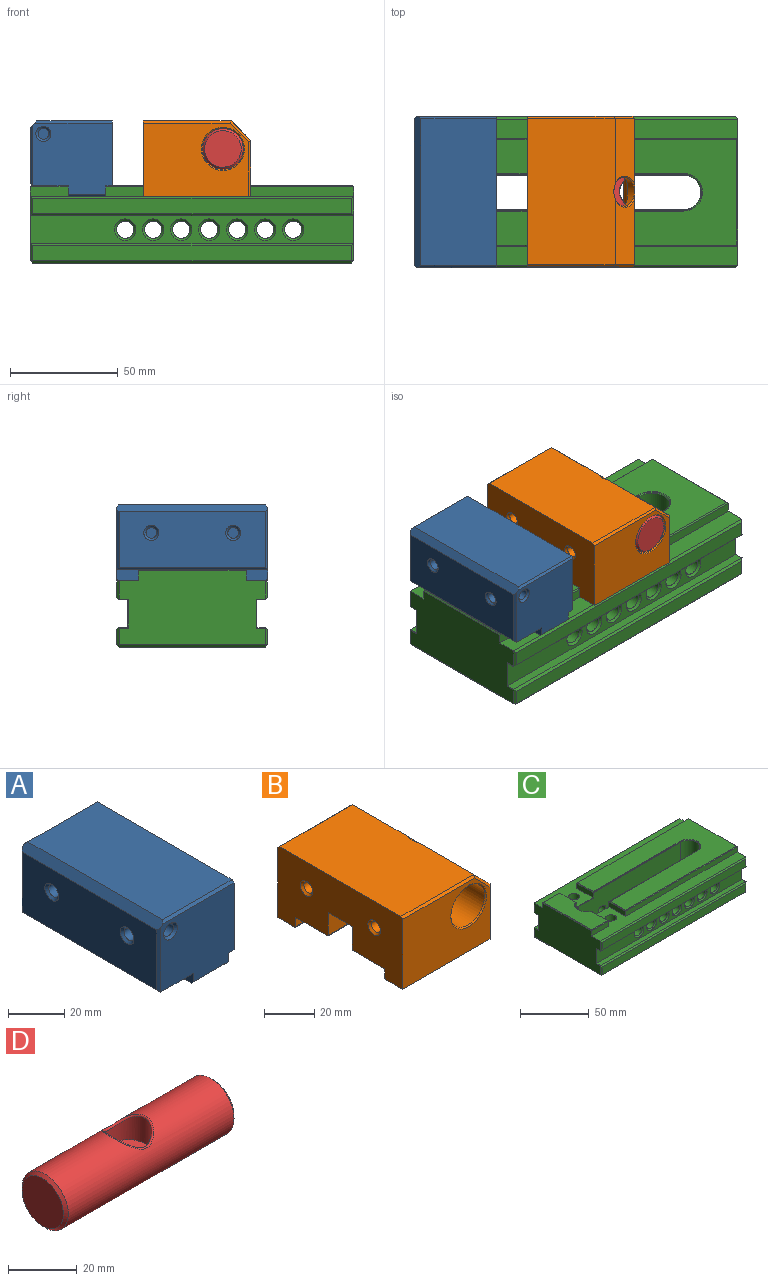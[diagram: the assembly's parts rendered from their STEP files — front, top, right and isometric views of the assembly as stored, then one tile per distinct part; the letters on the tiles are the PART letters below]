
ASSEMBLY  parts=4 mates=3
PART A: 42 faces, bbox 38x70x35 mm
  f0: plane 70x16.5mm, normal (0,0,-1), area 1155mm2, adj f1,f8,f9,f39
  f1: plane 70x4.8mm, normal (-1,0,0), area 335mm2, adj f0,f2,f8,f9,f40,f41
  f2: plane 68x17.5mm, normal (0,0,-1), area 1113mm2, adj f1,f3,f31,f32,f40,f41
  f3: plane 70x4.8mm, normal (1,0,0), area 335mm2, adj f2,f4,f8,f9,f40,f41
  f4: plane 70x3mm, normal (0,0,-1), area 210mm2, adj f3,f5,f8,f9
  f5: plane 70x30.2mm, normal (1,0,0), area 2036mm2, adj f4,f6,f8,f9,f11,f12,f33,f34
  f6: plane 68x35mm, normal (0,0,1), area 2380mm2, adj f5,f10,f11,f12
  f7: plane 68x26.2mm, normal (-1,0,0), area 1704.6mm2, adj f10,f13,f14,f37,f38,f39
  f8: plane 37x33mm, normal (0,1,0), area 1107.9mm2, adj f0,f1,f3,f4,f5,f10,f11,f13
  f9: plane 37x33mm, normal (0,-1,0), area 1107.9mm2, adj f0,f1,f3,f4,f5,f10,f12,f14
  f10: plane 70x3mm, normal (-0.71,0,0.71), area 294.2mm2, adj f6,f7,f8,f9,f11,f12,f13,f14
  f11: plane 36x1mm, normal (0,0.71,0.71), area 50.2mm2, adj f5,f6,f8,f10
  f12: plane 36x1mm, normal (0,-0.71,0.71), area 50.2mm2, adj f5,f6,f9,f10
  f13: plane 28.2x1mm, normal (-0.71,0.71,0), area 38.5mm2, adj f7,f8,f10,f39
  f14: plane 28.2x1mm, normal (-0.71,-0.71,0), area 38.5mm2, adj f7,f9,f10,f39
  f15: cylinder r=2.5mm len=14mm, axis (0,-1,0), area 219.9mm2, adj f16,f35
  f16: plane 5x5mm, normal (0,-1,0), area 19.6mm2, adj f15
  f17: cylinder r=2.5mm len=14mm, axis (0,-1,0), area 219.9mm2, adj f18,f36
  f18: plane 5x5mm, normal (0,1,0), area 19.6mm2, adj f17
  f19: cylinder r=2.5mm len=18.18mm, axis (0,0,-1), area 285.5mm2, adj f20,f32
  f20: plane 5x5mm, normal (0,0,-1), area 19.6mm2, adj f19
  f21: cylinder r=2.5mm len=18.18mm, axis (0,0,-1), area 285.5mm2, adj f22,f31
  f22: plane 5x5mm, normal (0,0,-1), area 19.6mm2, adj f21
  f23: cylinder r=2.5mm len=14mm, axis (1,0,0), area 219.9mm2, adj f24,f33
  f24: plane 5x5mm, normal (1,0,0), area 19.6mm2, adj f23
  f25: cylinder r=2.5mm len=14mm, axis (1,0,0), area 219.9mm2, adj f26,f34
  f26: plane 5x5mm, normal (1,0,0), area 19.6mm2, adj f25
  f27: cylinder r=2.5mm len=7mm, axis (1,0,0), area 110mm2, adj f28,f38
  f28: plane 5x5mm, normal (-1,0,0), area 19.6mm2, adj f27
  f29: cylinder r=2.5mm len=7mm, axis (1,0,0), area 110mm2, adj f30,f37
  f30: plane 5x5mm, normal (-1,0,0), area 19.6mm2, adj f29
  f31: cone r=3.5mm half-angle=45deg, axis (0,0,-1), area 26.7mm2, adj f2,f21
  f32: cone r=3.5mm half-angle=45deg, axis (0,0,-1), area 26.7mm2, adj f2,f19
  f33: cone r=2.5mm half-angle=45deg, axis (1,0,0), area 26.7mm2, adj f5,f23
  f34: cone r=2.5mm half-angle=45deg, axis (1,0,0), area 26.7mm2, adj f5,f25
  f35: cone r=2.5mm half-angle=45deg, axis (0,-1,0), area 26.7mm2, adj f9,f15
  f36: cone r=3.5mm half-angle=45deg, axis (0,1,0), area 26.7mm2, adj f8,f17
  f37: cone r=2.5mm half-angle=45deg, axis (-1,0,0), area 26.7mm2, adj f7,f29
  f38: cone r=2.5mm half-angle=45deg, axis (-1,0,0), area 26.7mm2, adj f7,f27
  f39: plane 70x1mm, normal (-0.71,0,-0.71), area 97.6mm2, adj f0,f7,f13,f14
  f40: plane 17.5x1mm, normal (0,0.71,-0.71), area 24.7mm2, adj f1,f2,f3,f8
  f41: plane 17.5x1mm, normal (0,-0.71,-0.71), area 24.7mm2, adj f1,f2,f3,f9
PART B: 38 faces, bbox 50.5x70x35.6 mm
  f0: plane 30.91x9.19mm, normal (0.71,0,0.71), area 362.7mm2, adj f3,f6,f23,f31
  f1: plane 30.91x9.19mm, normal (0.71,0,0.71), area 362.7mm2, adj f3,f6,f20,f31
  f2: plane 50x9.5mm, normal (0,0,-1), area 474.5mm2, adj f4,f6,f9,f19,f24
  f3: plane 68x40.81mm, normal (0,0,1), area 2772.4mm2, adj f0,f1,f4,f18,f21,f31
  f4: plane 70x35mm, normal (-1,0,0), area 1967.6mm2, adj f2,f3,f5,f8,f9,f10,f11,f13
  f5: plane 50x9.5mm, normal (0,0,-1), area 474.5mm2, adj f4,f6,f8,f22,f25
  f6: plane 68x25.81mm, normal (1,0,0), area 1348.4mm2, adj f0,f1,f2,f5,f10,f12,f13,f14
  f7: cylinder r=9.5mm len=69mm, axis (0,-1,0), area 3721.9mm2, adj f10,f11,f12,f13,f28,f29,f30
  f8: plane 49x34mm, normal (0,1,0), area 1314.8mm2, adj f4,f5,f21,f22,f23,f28
  f9: plane 49x34mm, normal (0,-1,0), area 1314.8mm2, adj f2,f4,f18,f19,f20,f29
  f10: plane 50x10.93mm, normal (0,-1,0), area 504mm2, adj f4,f6,f7,f11,f12,f26
  f11: plane 29.31x13.5mm, normal (0,0,-1), area 395.6mm2, adj f4,f7,f10,f13
  f12: plane 13.5x5.31mm, normal (0,0,-1), area 71.6mm2, adj f6,f7,f10,f13
  f13: plane 50x10.93mm, normal (0,1,0), area 504mm2, adj f4,f6,f7,f11,f12,f27
  f14: plane 50x4.5mm, normal (0,1,0), area 225mm2, adj f4,f6,f17,f24
  f15: plane 50x4.5mm, normal (0,-1,0), area 225mm2, adj f4,f6,f16,f25
  f16: plane 50x17.75mm, normal (0,0,-1), area 887.5mm2, adj f4,f6,f15,f26
  f17: plane 50x17.75mm, normal (0,0,-1), area 887.5mm2, adj f4,f6,f14,f27
  f18: plane 40.81x1mm, normal (0,-0.71,0.71), area 57.4mm2, adj f3,f4,f9,f20
  f19: plane 25.81x1mm, normal (0.71,-0.71,0), area 36.2mm2, adj f2,f6,f9,f20
  f20: plane 9.61x9.61mm, normal (0.5,-0.71,0.5), area 17.8mm2, adj f1,f9,f18,f19
  f21: plane 40.81x1mm, normal (0,0.71,0.71), area 57.4mm2, adj f3,f4,f8,f23
  f22: plane 25.81x1mm, normal (0.71,0.71,0), area 36.2mm2, adj f5,f6,f8,f23
  f23: plane 9.61x9.61mm, normal (0.5,0.71,0.5), area 17.8mm2, adj f0,f8,f21,f22
  f24: cylinder r=0.5mm len=50mm, axis (1,0,0), area 39.3mm2, adj f2,f4,f6,f14
  f25: cylinder r=0.5mm len=50mm, axis (-1,0,0), area 39.3mm2, adj f4,f5,f6,f15
  f26: cylinder r=0.5mm len=50mm, axis (-1,0,0), area 39.3mm2, adj f4,f6,f10,f16
  f27: cylinder r=0.5mm len=50mm, axis (-1,0,0), area 39.3mm2, adj f4,f6,f13,f17
  f28: cone r=10mm half-angle=45deg, axis (0,1,0), area 43.3mm2, adj f7,f8
  f29: cone r=9.5mm half-angle=45deg, axis (0,-1,0), area 43.3mm2, adj f7,f9
  f30: cylinder r=6.75mm len=13.5mm, axis (0.71,0,0.71), area 137mm2, adj f7,f31
  f31: cone r=6.75mm half-angle=45deg, axis (0.71,0,0.71), area 26.4mm2, adj f0,f1,f3,f6,f30
  f32: cylinder r=2.5mm len=14mm, axis (-1,0,0), area 219.9mm2, adj f33,f36
  f33: plane 5x5mm, normal (-1,0,0), area 19.6mm2, adj f32
  f34: cylinder r=2.5mm len=14mm, axis (-1,0,0), area 219.9mm2, adj f35,f37
  f35: plane 5x5mm, normal (-1,0,0), area 19.6mm2, adj f34
  f36: cone r=3.5mm half-angle=45deg, axis (-1,0,0), area 26.7mm2, adj f4,f32
  f37: cone r=3.5mm half-angle=45deg, axis (-1,0,0), area 26.7mm2, adj f4,f34
PART C: 125 faces, bbox 150x70x36 mm
  f0: plane 150x26.23mm, normal (0,0,1), area 1594.1mm2, adj f12,f13,f28,f29,f30,f31,f44,f79
  f1: plane 150x26.23mm, normal (0,0,1), area 1594.1mm2, adj f3,f4,f16,f17,f28,f29,f43,f74
  f2: plane 148x68mm, normal (0,0,-1), area 7568.5mm2, adj f53,f54,f55,f56,f57,f58,f60,f67
  f3: plane 17.47x4.73mm, normal (1,0,0), area 78.5mm2, adj f1,f16,f42,f86,f96
  f4: plane 17x4.7mm, normal (-1,0,0), area 76.5mm2, adj f1,f17,f39,f89,f95
  f5: cylinder r=4mm len=21mm, axis (0,-1,0), area 527.8mm2, adj f39,f111
  f6: cylinder r=4mm len=21mm, axis (0,-1,0), area 527.8mm2, adj f39,f112
  f7: cylinder r=4mm len=21mm, axis (0,-1,0), area 527.8mm2, adj f39,f113
  f8: cylinder r=4mm len=21mm, axis (0,-1,0), area 527.8mm2, adj f39,f114
  f9: cylinder r=4mm len=21mm, axis (0,-1,0), area 527.8mm2, adj f39,f115
  f10: cylinder r=4mm len=21mm, axis (0,-1,0), area 527.8mm2, adj f39,f116
  f11: cylinder r=4mm len=21mm, axis (0,-1,0), area 527.8mm2, adj f40,f41,f124
  f12: plane 17.5x4.5mm, normal (0,1,0), area 78.7mm2, adj f0,f28,f30,f81
  f13: plane 115x4.5mm, normal (0,1,0), area 517.5mm2, adj f0,f29,f31,f90
  f14: plane 49x16.5mm, normal (0,0,1), area 742.6mm2, adj f81,f82,f83,f84,f85,f86
  f15: plane 114x49mm, normal (0,0,1), area 3908.5mm2, adj f87,f88,f89,f90,f91,f92,f93,f94
  f16: plane 17.5x4.5mm, normal (0,-1,0), area 78.7mm2, adj f1,f3,f28,f84
  f17: plane 115x4.5mm, normal (0,-1,0), area 517.5mm2, adj f1,f4,f29,f87
  f18: plane 149.6x4mm, normal (0,0,-1), area 598.4mm2, adj f27,f78,f99,f108
  f19: plane 148x7mm, normal (0,1,0), area 1036mm2, adj f77,f78,f79,f80
  f20: plane 148x7mm, normal (0,-1,0), area 1036mm2, adj f73,f74,f75,f76
  f21: plane 149.6x4mm, normal (0,0,-1), area 598.4mm2, adj f22,f75,f104,f107
  f22: plane 149.6x13mm, normal (0,-1,0), area 1395mm2, adj f21,f23,f103,f106,f111,f112,f113,f114
  f23: plane 149.6x4mm, normal (0,0,1), area 598.4mm2, adj f22,f62,f102,f105
  f24: plane 148x7mm, normal (0,-1,0), area 1036mm2, adj f59,f62,f66,f67
  f25: plane 148x7mm, normal (0,1,0), area 1036mm2, adj f61,f65,f68,f69
  f26: plane 149.6x4mm, normal (0,0,1), area 598.4mm2, adj f27,f65,f101,f110
  f27: plane 149.6x13mm, normal (0,1,0), area 1395mm2, adj f18,f26,f100,f109,f118,f119,f120,f121
  f28: plane 68x34.5mm, normal (-1,0,0), area 2152.4mm2, adj f0,f1,f12,f16,f66,f69,f72,f76
  f29: plane 68x34.5mm, normal (1,0,0), area 2152.4mm2, adj f0,f1,f13,f17,f59,f60,f61,f73
  f30: plane 17.47x4.73mm, normal (1,0,0), area 78.5mm2, adj f0,f12,f42,f83,f98
  f31: plane 17x4.7mm, normal (-1,0,0), area 76.5mm2, adj f0,f13,f41,f92,f97
  f32: cylinder r=4mm len=21mm, axis (0,-1,0), area 527.8mm2, adj f41,f118
  f33: cylinder r=4mm len=21mm, axis (0,-1,0), area 527.8mm2, adj f41,f119
  f34: cylinder r=4mm len=21mm, axis (0,-1,0), area 527.8mm2, adj f41,f120
  f35: cylinder r=4mm len=21mm, axis (0,-1,0), area 527.8mm2, adj f41,f121
  f36: cylinder r=4mm len=21mm, axis (0,-1,0), area 527.8mm2, adj f41,f122
  f37: cylinder r=4mm len=21mm, axis (0,-1,0), area 527.8mm2, adj f41,f123
  f38: cylinder r=4mm len=21mm, axis (0,-1,0), area 527.8mm2, adj f39,f40,f117
  f39: plane 104.74x34.5mm, normal (0,1,0), area 3196.2mm2, adj f4,f5,f6,f7,f8,f9,f10,f38
  f40: cylinder r=8mm len=34.5mm, axis (0,0,-1), area 867.2mm2, adj f11,f38,f39,f41,f51,f55
  f41: plane 104.76x34.5mm, normal (0,-1,0), area 3196.7mm2, adj f11,f31,f32,f33,f34,f35,f36,f37
  f42: cylinder r=8mm len=34.5mm, axis (0,0,-1), area 841.9mm2, adj f3,f30,f39,f41,f49,f58,f96,f98
  f43: cylinder r=4mm len=23mm, axis (0,0,-1), area 578.1mm2, adj f1,f48
  f44: cylinder r=4mm len=23mm, axis (0,0,-1), area 578.1mm2, adj f0,f46
  f45: cylinder r=6.5mm len=13mm, axis (0,0,-1), area 285.9mm2, adj f46,f53
  f46: plane 13x13mm, normal (0,0,-1), area 82.5mm2, adj f44,f45
  f47: cylinder r=6.5mm len=13mm, axis (0,0,-1), area 285.9mm2, adj f48,f54
  f48: plane 13x13mm, normal (0,0,-1), area 82.5mm2, adj f43,f47
  f49: cone r=8mm half-angle=45deg, axis (0,0,1), area 10mm2, adj f42,f83,f85,f86
  f50: plane 89.88x0.35mm, normal (0,-0.71,0.71), area 44.9mm2, adj f41,f51,f92,f94
  f51: cone r=8mm half-angle=45deg, axis (0,0,1), area 13mm2, adj f40,f50,f52,f93
  f52: plane 89.86x0.35mm, normal (0,0.71,0.71), area 44.8mm2, adj f39,f51,f89,f91
  f53: cone r=7.5mm half-angle=45deg, axis (0,0,-1), area 62.2mm2, adj f2,f45
  f54: cone r=7.5mm half-angle=45deg, axis (0,0,-1), area 62.2mm2, adj f2,f47
  f55: cone r=9mm half-angle=45deg, axis (0,0,-1), area 38.1mm2, adj f2,f40,f56,f57
  f56: plane 104.74x1mm, normal (0,0.71,-0.71), area 148.1mm2, adj f2,f39,f55,f58
  f57: plane 104.76x1mm, normal (0,-0.71,-0.71), area 148.1mm2, adj f2,f41,f55,f58
  f58: cone r=8mm half-angle=45deg, axis (0,0,-1), area 37.8mm2, adj f2,f42,f56,f57
  f59: plane 7.97x1.03mm, normal (0.71,-0.71,0), area 10.6mm2, adj f24,f29,f62,f63,f102
  f60: plane 68x1mm, normal (0.71,0,-0.71), area 96.2mm2, adj f2,f29,f63,f64
  f61: plane 7.97x1.03mm, normal (0.71,0.71,0), area 10.6mm2, adj f25,f29,f64,f65,f101
  f62: plane 149.91x1.03mm, normal (0,-0.71,0.71), area 210.7mm2, adj f23,f24,f59,f66,f102,f105
  f63: plane 1x1mm, normal (0.58,-0.58,-0.58), area 0.9mm2, adj f59,f60,f67
  f64: plane 1x1mm, normal (0.58,0.58,-0.58), area 0.9mm2, adj f60,f61,f68
  f65: plane 149.91x1.03mm, normal (0,0.71,0.71), area 210.7mm2, adj f25,f26,f61,f69,f101,f110
  f66: plane 7.97x1.03mm, normal (-0.71,-0.71,0), area 10.6mm2, adj f24,f28,f62,f70,f105
  f67: plane 148x1mm, normal (0,-0.71,-0.71), area 209.3mm2, adj f2,f24,f63,f70
  f68: plane 148x1mm, normal (0,0.71,-0.71), area 209.3mm2, adj f2,f25,f64,f71
  f69: plane 7.97x1.03mm, normal (-0.71,0.71,0), area 10.6mm2, adj f25,f28,f65,f71,f110
  f70: plane 1x1mm, normal (-0.58,-0.58,-0.58), area 0.9mm2, adj f66,f67,f72
  f71: plane 1x1mm, normal (-0.58,0.58,-0.58), area 0.9mm2, adj f68,f69,f72
  f72: plane 68x1mm, normal (-0.71,0,-0.71), area 96.2mm2, adj f2,f28,f70,f71
  f73: plane 8.97x1.03mm, normal (0.71,-0.71,0), area 11.3mm2, adj f20,f29,f74,f75,f104
  f74: plane 150x1mm, normal (0,-0.71,0.71), area 210.7mm2, adj f1,f20,f73,f76
  f75: plane 149.91x1.03mm, normal (0,-0.71,-0.71), area 210.7mm2, adj f20,f21,f73,f76,f104,f107
  f76: plane 8.97x1.03mm, normal (-0.71,-0.71,0), area 11.3mm2, adj f20,f28,f74,f75,f107
  f77: plane 8.97x1.03mm, normal (0.71,0.71,0), area 11.3mm2, adj f19,f29,f78,f79,f99
  f78: plane 149.91x1.03mm, normal (0,0.71,-0.71), area 210.7mm2, adj f18,f19,f77,f80,f99,f108
  f79: plane 150x1mm, normal (0,0.71,0.71), area 210.7mm2, adj f0,f19,f77,f80
  f80: plane 8.97x1.03mm, normal (-0.71,0.71,0), area 11.3mm2, adj f19,f28,f78,f79,f108
  f81: plane 17.5x0.5mm, normal (0,0.71,0.71), area 12mm2, adj f12,f14,f82,f83
  f82: plane 50x0.5mm, normal (-0.71,0,0.71), area 35mm2, adj f14,f28,f81,f84
  f83: plane 17.45x0.5mm, normal (0.71,0,0.71), area 12mm2, adj f14,f30,f49,f81,f85
  f84: plane 17.5x0.5mm, normal (0,-0.71,0.71), area 12mm2, adj f14,f16,f82,f86
  f85: cone r=8.71mm half-angle=67.5deg, axis (0,0,1), area 7.9mm2, adj f14,f49,f83,f86
  f86: plane 17.45x0.5mm, normal (0.71,0,0.71), area 12mm2, adj f3,f14,f49,f84,f85
  f87: plane 115x0.5mm, normal (0,-0.71,0.71), area 81mm2, adj f15,f17,f88,f89
  f88: plane 50x0.5mm, normal (0.71,0,0.71), area 35mm2, adj f15,f29,f87,f90
  f89: plane 17x0.5mm, normal (-0.71,0,0.71), area 11.6mm2, adj f4,f15,f52,f87,f91
  f90: plane 115x0.5mm, normal (0,0.71,0.71), area 81mm2, adj f13,f15,f88,f92
  f91: plane 89.51x0.35mm, normal (0,0.38,0.92), area 34.2mm2, adj f15,f52,f89,f93
  f92: plane 17x0.5mm, normal (-0.71,0,0.71), area 11.6mm2, adj f15,f31,f50,f90,f94
  f93: cone r=8.71mm half-angle=67.5deg, axis (0,0,1), area 10.4mm2, adj f15,f51,f91,f94
  f94: plane 89.53x0.35mm, normal (0,-0.38,0.92), area 34.2mm2, adj f15,f50,f92,f93
  f95: cylinder r=0.2mm len=14.88mm, axis (-1,0,0), area 4.7mm2, adj f1,f4,f39,f96
  f96: torus R=8.2mm, axis (0,0,1), area 0.8mm2, adj f1,f3,f42,f95
  f97: cylinder r=0.2mm len=14.88mm, axis (1,0,0), area 4.7mm2, adj f0,f31,f41,f98
  f98: torus R=8.2mm, axis (0,0,1), area 0.8mm2, adj f0,f30,f42,f97
  f99: cylinder r=0.2mm len=4.26mm, axis (0,1,0), area 1.3mm2, adj f18,f29,f77,f78,f100
  f100: cylinder r=0.2mm len=13.4mm, axis (0,0,1), area 4.1mm2, adj f27,f29,f99,f101
  f101: cylinder r=0.2mm len=4.26mm, axis (0,-1,0), area 1.3mm2, adj f26,f29,f61,f65,f100
  f102: cylinder r=0.2mm len=4.26mm, axis (0,-1,0), area 1.3mm2, adj f23,f29,f59,f62,f103
  f103: cylinder r=0.2mm len=13.4mm, axis (0,0,-1), area 4.1mm2, adj f22,f29,f102,f104
  f104: cylinder r=0.2mm len=4.26mm, axis (0,1,0), area 1.3mm2, adj f21,f29,f73,f75,f103
  f105: cylinder r=0.2mm len=4.26mm, axis (0,1,0), area 1.3mm2, adj f23,f28,f62,f66,f106
  f106: cylinder r=0.2mm len=13.4mm, axis (0,0,1), area 4.1mm2, adj f22,f28,f105,f107
  f107: cylinder r=0.2mm len=4.26mm, axis (0,-1,0), area 1.3mm2, adj f21,f28,f75,f76,f106
  f108: cylinder r=0.2mm len=4.26mm, axis (0,-1,0), area 1.3mm2, adj f18,f28,f78,f80,f109
  f109: cylinder r=0.2mm len=13.4mm, axis (0,0,-1), area 4.1mm2, adj f27,f28,f108,f110
  f110: cylinder r=0.2mm len=4.26mm, axis (0,1,0), area 1.3mm2, adj f26,f28,f65,f69,f109
  f111: cone r=4mm half-angle=45deg, axis (0,-1,0), area 40mm2, adj f5,f22
  f112: cone r=4mm half-angle=45deg, axis (0,-1,0), area 40mm2, adj f6,f22
  f113: cone r=4mm half-angle=45deg, axis (0,-1,0), area 40mm2, adj f7,f22
  f114: cone r=4mm half-angle=45deg, axis (0,-1,0), area 40mm2, adj f8,f22
  f115: cone r=4mm half-angle=45deg, axis (0,-1,0), area 40mm2, adj f9,f22
  f116: cone r=4mm half-angle=45deg, axis (0,-1,0), area 40mm2, adj f10,f22
  f117: cone r=4mm half-angle=45deg, axis (0,-1,0), area 40mm2, adj f22,f38
  f118: cone r=5mm half-angle=45deg, axis (0,1,0), area 40mm2, adj f27,f32
  f119: cone r=5mm half-angle=45deg, axis (0,1,0), area 40mm2, adj f27,f33
  f120: cone r=5mm half-angle=45deg, axis (0,1,0), area 40mm2, adj f27,f34
  f121: cone r=5mm half-angle=45deg, axis (0,1,0), area 40mm2, adj f27,f35
  f122: cone r=5mm half-angle=45deg, axis (0,1,0), area 40mm2, adj f27,f36
  f123: cone r=5mm half-angle=45deg, axis (0,1,0), area 40mm2, adj f27,f37
  f124: cone r=5mm half-angle=45deg, axis (0,1,0), area 40mm2, adj f11,f27
PART D: 10 faces, bbox 70x19x19 mm
  f0: cylinder r=9.5mm len=68mm, axis (1,0,0), area 3817.4mm2, adj f3,f4,f8,f9
  f1: plane 17x17mm, normal (1,0,0), area 227mm2, adj f3
  f2: plane 17x17mm, normal (-1,0,0), area 227mm2, adj f4
  f3: cone r=8.5mm half-angle=45deg, axis (-1,0,0), area 80mm2, adj f0,f1
  f4: cone r=9.5mm half-angle=45deg, axis (1,0,0), area 80mm2, adj f0,f2
  f5: cylinder r=6.75mm len=13.5mm, axis (0,0,-1), area 309mm2, adj f6,f9
  f6: plane 13.5x13.5mm, normal (0,0,1), area 110mm2, adj f5,f7
  f7: cylinder r=3.25mm len=9mm, axis (0,0,1), area 175.5mm2, adj f6,f8
  f8: bspline ~7.93x7.51mm, area 19.7mm2, adj f0,f7
  f9: bspline ~15.31x14.51mm, area 47.1mm2, adj f0,f5
PLACE A t=(-70.84,-41.75,41.35)mm
PLACE B t=(-56.49,-41.5,32.17)mm
PLACE C t=(41.16,-6.75,1.17)mm fixed
PLACE D rot(axis=(-0.58,0.58,-0.58),120deg) t=(-19.49,-41.5,54.17)mm
MATE fastened A.f21 <-> C.f43  axis (0,0,-1) through (-82.59,-25.75,32.17)mm
MATE slider C.f29 <-> B.f6  axis (1,0,0) through (41.16,-36.25,32.17)mm
MATE fastened D.f0 <-> B.f7  axis (0,-1,0) through (-19.49,-6.5,54.17)mm
